# Revit family: Lighting-Suspended-Philips_Ledalite-TruGroove_LED
name_source: partatom
category: Lighting Fixtures
revit_build: Autodesk Revit 2017 (Build: 20160720_1515(x64)
units: mm (PartAtom-declared; Revit-internal decimal feet)

## family parameters
Cut with Voids When Loaded = No
Host = Face
Light Source = Yes
OmniClass Number = 23.80.70.11.14
OmniClass Title = General Luminaries, Directional
Part Type = Normal
Room Calculation Point = No
Round Connector Dimension = Use Diameter
Shared = No

## types (66) — shared parameters
Assembly Code = D5020200
Color Filter = 16777215
Default Elevation = 48"
Depth = 5"
Dimming Lamp Color Temperature Shift = <None>
Emit Shape Visible in Rendering = No
Emit from Rectangle Length = 48"
Emit from Rectangle Width = 3 7/32"
End Cap Depth = 3/16"
Housing Material Finish = Powder Coat-Signify-Titanium
Lamp = LED
Last Updated = 6/17/2015
Length = 48"
Lens Material Finish = Acrylic-Signify-White, Translucent
Manufacturer = Ledalite
Photometry Comments = Candela values are absolute.
Product Family = TruGroove
Product Page URL = http://www.lightingproducts.philips.com
Suspension Distance = 12"
Tilt Angle = -90.00°
URL = https://www.signify.com
Voltage = 120 V
Width = 3 7/32"
eCatalog URL = www.ledalite.com

## per-type parameters (varying)
| type | Apparent Load | Catalog Number | Description | Model | Photometric Web File |
| 2901LAEQN4 | 35 VA | 2901LAEQN4 | TruGroove Suspended Direct, LED, 4000K, 3200 Nominal Delivered Lumens, Symmetric MesoOptics, 4' | 2901LAEQN4 | 29x1LAEQN.ies |
| 2901LAEWN4 | 36 VA | 2901LAEWN4 | TruGroove Suspended Direct, LED, 4000K, 3200 Nominal Delivered Lumens, Asymmetric MesoOptics, 4' | 2901LAEWN4 | 29x1LAEWN.ies |
| 2901LAGQN4 | 24 VA | 2901LAGQN4 | TruGroove Suspended Direct, LED, 4000K, 2300 Nominal Delivered Lumens, Symmetric MesoOptics, 4' | 2901LAGQN4 | 29x1LAGQN.ies |
| 2901LAGWN4 | 24 VA | 2901LAGWN4 | TruGroove Suspended Direct, LED, 4000K, 2300 Nominal Delivered Lumens, Asymmetric MesoOptics, 4' | 2901LAGWN4 | 29x1LAGWN.ies |
| 2901LAKQN4 | 15 VA | 2901LAKQN4 | TruGroove Suspended Direct, LED, 4000K, 1500 Nominal Delivered Lumens, Symmetric MesoOptics, 4' | 2901LAKQN4 | 29x1LAKQN.ies |
| 2901LAKWN4 | 15 VA | 2901LAKWN4 | TruGroove Suspended Direct, LED, 4000K, 1500 Nominal Delivered Lumens, Asymmetric MesoOptics, 4' | 2901LAKWN4 | 29x1LAKWN.ies |
| 2901LBEQN4 | 35 VA | 2901LBEQN4 | TruGroove Suspended Direct, LED, 3500K, 3200 Nominal Delivered Lumens, Symmetric MesoOptics, 4' | 2901LBEQN4 | 29x1LBEQN.ies |
| 2901LBEWN4 | 35 VA | 2901LBEWN4 | TruGroove Suspended Direct, LED, 3500K, 3200 Nominal Delivered Lumens, Asymmetric MesoOptics, 4' | 2901LBEWN4 | 29x1LBEWN.ies |
| 2901LBGQN4 | 24 VA | 2901LBGQN4 | TruGroove Suspended Direct, LED, 3500K, 2300 Nominal Delivered Lumens, Symmetric MesoOptics, 4' | 2901LBGQN4 | 29x1LBGQN.ies |
| 2901LBGWN4 | 24 VA | 2911LBGWN4 | TruGroove Suspended Direct, LED, 3500K, 2300 Nominal Delivered Lumens, Asymmetric MesoOptics, 4' | 2911LBGWN4 | 29x1LBGWN.ies |
| 2901LBKQN4 | 15 VA | 2901LBKQN4 | TruGroove Suspended Direct, LED, 3500K, 1500 Nominal Delivered Lumens, Symmetric MesoOptics, 4' | 2901LBKQN4 | 29x1LBKQN.ies |
| 2901LBKWN4 | 15 VA | 2901LBKWN4 | TruGroove Suspended Direct, LED, 3500K, 1500 Nominal Delivered Lumens, Asymmetric MesoOptics, 4' | 2901LBKWN4 | 29x1LBKWN.ies |
| 2901LCEQN4 | 35 VA | 2901LCEQN4 | TruGroove Suspended Direct, LED, 3000K, 3200 Nominal Delivered Lumens, Symmetric MesoOptics, 4' | 2901LCEQN4 | 29x1LCEQN.ies |
| 2901LCEWN4 | 35 VA | 2901LCEWN4 | TruGroove Suspended Direct, LED, 3000K, 3200 Nominal Delivered Lumens, Asymmetric MesoOptics, 4' | 2901LCEWN4 | 29x1LCEWN.ies |
| 2901LCGQN4 | 24 VA | 2901LCGQN4 | TruGroove Suspended Direct, LED, 3000K, 2300 Nominal Delivered Lumens, Symmetric MesoOptics, 4' | 2901LCGQN4 | 29x1LCGQN.ies |
| 2901LCGWN4 | 24 VA | 2901LCGWN4 | TruGroove Suspended Direct, LED, 3000K, 2300 Nominal Delivered Lumens, Asymmetric MesoOptics, 4' | 2901LCGWN4 | 29x1LCGWN.ies |
| 2901LCKQN4 | 15 VA | 2901LCKQN4 | TruGroove Suspended Direct, LED, 3000K, 1500 Nominal Delivered Lumens, Symmetric MesoOptics, 4' | 2901LCKQN4 | 29x1LCKQN.ies |
| 2901LCKWN4 | 15 VA | 2901LCKWN4 | TruGroove Suspended Direct, LED, 3000K, 1500 Nominal Delivered Lumens, Asymmetric MesoOptics, 4' | 2901LCKWN4 | 29x1LCKWN.ies |
| 2903LACNQ4 | 41 VA | 2903LACNQ4 | TruGroove Suspended Indirect, LED, 4000K, 4800 Nominal Delivered Lumens, Symmetric MesoOptics, 4' | 2903LACNQ4 | 29x3LACNQ.ies |
| 2903LACNW4 | 41 VA | 2903LACNW4 | TruGroove Suspended Indirect, LED, 4000K, 4800 Nominal Delivered Lumens, Asymmetric MesoOptics, 4' | 2903LACNW4 | 29x3LACNW.ies |
| 2903LAENQ4 | 26 VA | 2903LAENQ4 | TruGroove Suspended Indirect, LED, 4000K, 3200 Nominal Delivered Lumens, Symmetric MesoOptics, 4' | 2903LAENQ4 | 29x3LAENQ.ies |
| 2903LAENW4 | 26 VA | 2903LAENW4 | TruGroove Suspended Indirect, LED, 4000K, 3200 Nominal Delivered Lumens, Asymmetric MesoOptics, 4' | 2903LAENW4 | 29x3LAENW.ies |
| 2903LBCNQ4 | 41 VA | 2903LBCNQ4 | TruGroove Suspended Indirect, LED, 3500K, 4800 Nominal Delivered Lumens, Symmetric MesoOptics, 4' | 2903LBCNQ4 | 29x3LBCNQ.ies |
| 2903LBCNW4 | 41 VA | 2903LBCNW4 | TruGroove Suspended Indirect, LED, 3500K, 4800 Nominal Delivered Lumens, Asymmetric MesoOptics, 4' | 2903LBCNW4 | 29x3LBCNW.ies |
| 2903LBENQ4 | 26 VA | 2903LBENQ4 | TruGroove Suspended Indirect, LED, 3500K, 3200 Nominal Delivered Lumens, Symmetric MesoOptics, 4' | 2903LBENQ4 | 29x3LBENQ.ies |
| 2903LBENW4 | 26 VA | 2903LBENW4 | TruGroove Suspended Indirect, LED, 3500K, 3200 Nominal Delivered Lumens, Asymmetric MesoOptics, 4' | 2903LBENW4 | 29x3LBENW.ies |
| 2903LCCNQ4 | 41 VA | 2903LCCNQ4 | TruGroove Suspended Indirect, LED, 3000K, 4800 Nominal Delivered Lumens, Symmetric MesoOptics, 4' | 2903LCCNQ4 | 29x3LCCNQ.ies |
| 2903LCCNW4 | 41 VA | 2903LCCNQ4 | TruGroove Suspended Indirect, LED, 3000K, 4800 Nominal Delivered Lumens, Asymmetric MesoOptics, 4' | 2903LCCNQ4 | 29x3LCCNQ.ies |
| 2903LCENQ4 | 26 VA | 2903LCENQ4 | TruGroove Suspended Indirect, LED, 3000K, 3200 Nominal Delivered Lumens, Symmetric MesoOptics, 4' | 2903LCENQ4 | 29x3LCENQ.ies |
| 2903LCENW4 | 26 VA | 2903LCENW4 | TruGroove Suspended Indirect, LED, 3000K, 3200 Nominal Delivered Lumens, Asymmetric MesoOptics, 4' | 2903LCENW4 | 29x3LCENW.ies |
| 2905LABQQ4 | 47 VA | 2905LABQQ4 | TruGroove Suspended Indirect/Direct, LED, 4000K, 5200 Nominal Delivered Lumens, Symmetric MesoOptics Top & Bottom, 4' | 2905LABQQ4 | 29x5LABQQ.ies |
| 2905LABWW4 | 47 VA | 2905LABWW4 | TruGroove Suspended Indirect/Direct, LED, 4000K, 5200 Nominal Delivered Lumens, Asymmetric MesoOptics Top and Bottom, 4' | 2905LABWW4 | 29x5LABWW.ies |
| 2905LACQQ4 | 41 VA | 2905LACQQ4 | TruGroove Suspended Indirect/Direct, LED, 4000K, 4600 Nominal Delivered Lumens, Symmetric MesoOptics Top & Bottom, 4' | 2905LACQQ4 | 29x5LACQQ.ies |
| 2905LACWW4 | 41 VA | 2905LACWW4 | TruGroove Suspended Indirect/Direct, LED, 4000K, 4600 Nominal Delivered Lumens, Asymmetric MesoOptics Top and Bottom, 4' | 2905LACWW4 | 29x5LACWW.ies |
| 2905LADQQ4 | 29 VA | 2905LADQQ4 | TruGroove Suspended Indirect/Direct, LED, 4000K, 3500 Nominal Delivered Lumens, Symmetric MesoOptics Top & Bottom, 4' | 2905LADQQ4 | 29x5LADQQ.ies |
| 2905LADWW4 | 29 VA | 2905LADWW4 | TruGroove Suspended Indirect/Direct, LED, 4000K, 3500 Nominal Delivered Lumens, Asymmetric MesoOptics Top and Bottom, 4' | 2905LADWW4 | 29x5LADWW.ies |
| 2905LBBQQ4 | 46 VA | 2905LBBQQ4 | TruGroove Suspended Indirect/Direct, LED, 3500K, 5200 Nominal Delivered Lumens, Symmetric MesoOptics Top & Bottom, 4' | 2905LBBQQ4 | 29x5LBBQQ.ies |
| 2905LBBWW4 | 46 VA | 2905LBBWW4 | TruGroove Suspended Indirect/Direct, LED, 3500K, 5200 Nominal Delivered Lumens, Asymmetric MesoOptics Top and Bottom, 4' | 2905LBBWW4 | 29x5LBBWW.ies |
| 2905LBCQQ4 | 41 VA | 2905LBCQQ4 | TruGroove Suspended Indirect/Direct, LED, 3500K, 4600 Nominal Delivered Lumens, Symmetric MesoOptics Top & Bottom, 4' | 2905LBCQQ4 | 29x5LBCQQ.ies |
| 2905LBCWW4 | 41 VA | 2905LBCWW4 | TruGroove Suspended Indirect/Direct, LED, 3500K, 4600 Nominal Delivered Lumens, Asymmetric MesoOptics Top and Bottom, 4' | 2905LBCWW4 | 29x5LBCWW.ies |
| 2905LBDQQ4 | 29 VA | 2905LBDQQ4 | TruGroove Suspended Indirect/Direct, LED, 3500K, 3500 Nominal Delivered Lumens, Symmetric MesoOptics Top & Bottom, 4' | 2905LBDQQ4 | 29x5LBDQQ.ies |
| 2905LBDWW4 | 29 VA | 2905LBDWW4 | TruGroove Suspended Indirect/Direct, LED, 3500K, 3500 Nominal Delivered Lumens, Asymmetric MesoOptics Top and Bottom, 4' | 2905LBDWW4 | 29x5LBDWW.ies |
| 2905LCBQQ4 | 46 VA | 2905LCBQQ4 | TruGroove Suspended Indirect/Direct, LED, 3000K, 5200 Nominal Delivered Lumens, Symmetric MesoOptics Top & Bottom, 4' | 2905LCBQQ4 | 29x5LCBQQ.ies |
| 2905LCBWW4 | 46 VA | 2905LCBWW4 | TruGroove Suspended Indirect/Direct, LED, 3000K, 5200 Nominal Delivered Lumens, Asymmetric MesoOptics Top and Bottom, 4' | 2905LCBWW4 | 29x5LCBWW.ies |
| 2905LCCQQ4 | 41 VA | 2905LCCQQ4 | TruGroove Suspended Indirect/Direct, LED, 3000K, 4600 Nominal Delivered Lumens, Symmetric MesoOptics Top & Bottom, 4' | 2905LCCQQ4 | 29x5LCCQQ.ies |
| 2905LCCWW4 | 41 VA | 2905LCCWW4 | TruGroove Suspended Indirect/Direct, LED, 3000K, 4600 Nominal Delivered Lumens, Asymmetric MesoOptics Top and Bottom, 4' | 2905LCCWW4 | 29x5LCCWW.ies |
| 2905LCDQQ4 | 29 VA | 2905LCDQQ4 | TruGroove Suspended Indirect/Direct, LED, 3000K, 3500 Nominal Delivered Lumens, Symmetric MesoOptics Top & Bottom, 4' | 2905LCDQQ4 | 29x5LCDQQ.ies |
| 2905LCDWW4 | 29 VA | 2905LCDWW4 | TruGroove Suspended Indirect/Direct, LED, 3000K, 3500 Nominal Delivered Lumens, Asymmetric MesoOptics Top and Bottom, 4' | 2905LCDWW4 | 29x5LCDWW.ies |
| 2906LABQQ4 | 51 VA | 2906LABQQ4 | TruGroove Suspended Direct/Indirect, LED, 4000K, 5200 Nominal Delivered Lumens, Symmetirc MesoOptics Top and Bottom, 4' | 2906LABQQ4 | 29x6LABQQ.ies |
| 2906LABWW4 | 51 VA | 2906LABWW4 | TruGroove Suspended Direct/Indirect, LED, 4000K, 5200 Nominal Delivered Lumens, Asymmetirc MesoOptics Top and Bottom, 4' | 2906LABWW4 | 29x6LABWW.ies |
| 2906LACQQ4 | 46 VA | 2906LACQQ4 | TruGroove Suspended Direct/Indirect, LED, 4000K, 4600 Nominal Delivered Lumens, Symmetirc MesoOptics Top and Bottom, 4' | 2906LACQQ4 | 29x6LACQQ.ies |
| 2906LACWW4 | 46 VA | 2906LACWW4 | TruGroove Suspended Direct/Indirect, LED, 4000K, 4600 Nominal Delivered Lumens, Asymmetirc MesoOptics Top and Bottom, 4' | 2906LACWW4 | 29x6LACWW.ies |
| 2906LADQQ4 | 35 VA | 2906LADQQ4 | TruGroove Suspended Direct/Indirect, LED, 4000K, 3500 Nominal Delivered Lumens, Symmetirc MesoOptics Top and Bottom, 4' | 2906LADQQ4 | 29x6LADQQ.ies |
| 2906LADWW4 | 35 VA | 2906LADWW4 | TruGroove Suspended Direct/Indirect, LED, 4000K, 3500 Nominal Delivered Lumens, Asymmetirc MesoOptics Top and Bottom, 4' | 2906LADWW4 | 29x6LADWW.ies |
| 2906LBBQQ4 | 50 VA | 2906LBBQQ4 | TruGroove Suspended Direct/Indirect, LED, 3500K, 5200 Nominal Delivered Lumens, Symmetirc MesoOptics Top and Bottom, 4' | 2906LBBQQ4 | 29x6LBBQQ.ies |
| 2906LBBWW4 | 50 VA | 2906LBBWW4 | TruGroove Suspended Direct/Indirect, LED, 3500K, 5200 Nominal Delivered Lumens, Asymmetirc MesoOptics Top and Bottom, 4' | 2906LBBWW4 | 29x6LBBWW.ies |
| 2906LBCQQ4 | 46 VA | 2906LBCQQ4 | TruGroove Suspended Direct/Indirect, LED, 3500K, 4600 Nominal Delivered Lumens, Symmetirc MesoOptics Top and Bottom, 4' | 2906LBCQQ4 | 29x6LBCQQ.ies |
| 2906LBCWW4 | 46 VA | 2906LBCWW4 | TruGroove Suspended Direct/Indirect, LED, 3500K, 4600 Nominal Delivered Lumens, Asymmetirc MesoOptics Top and Bottom, 4' | 2906LBCWW4 | 29x6LBCWW.ies |
| 2906LBDQQ4 | 35 VA | 2906LBDQQ4 | TruGroove Suspended Direct/Indirect, LED, 3500K, 3500 Nominal Delivered Lumens, Symmetirc MesoOptics Top and Bottom, 4' | 2906LBDQQ4 | 29x6LBDQQ.ies |
| 2906LBDWW4 | 35 VA | 2906LBDWW4 | TruGroove Suspended Direct/Indirect, LED, 3500K, 3500 Nominal Delivered Lumens, Asymmetirc MesoOptics Top and Bottom, 4' | 2906LBDWW4 | 29x6LBDWW.ies |
| 2906LCBQQ4 | 50 VA | 2906LCBQQ1 | TruGroove Suspended Direct/Indirect, LED, 3000K, 5200 Nominal Delivered Lumens, Symmetirc MesoOptics Top and Bottom, 4' | 2906LCBQQ1 | 29x6LCBQQ.ies |
| 2906LCBWW4 | 50 VA | 2906LCBWW4 | TruGroove Suspended Direct/Indirect, LED, 3000K, 5200 Nominal Delivered Lumens, Asymmetirc MesoOptics Top and Bottom, 4' | 2906LCBWW4 | 29x6LCBWW.ies |
| 2906LCCQQ4 | 46 VA | 2906LCCQQ4 | TruGroove Suspended Direct/Indirect, LED, 3000K, 4600 Nominal Delivered Lumens, Symmetirc MesoOptics Top and Bottom, 4' | 2906LCCQQ4 | 29x6LCCQQ.ies |
| 2906LCCWW4 | 46 VA | 2906LCCWW4 | TruGroove Suspended Direct/Indirect, LED, 3000K, 4600 Nominal Delivered Lumens, Asymmetirc MesoOptics Top and Bottom, 4' | 2906LCCWW4 | 29x6LCCWW.ies |
| 2906LCDQQ4 | 35 VA | 2906LCDQQ4 | TruGroove Suspended Direct/Indirect, LED, 3000K, 3500 Nominal Delivered Lumens, Symmetirc MesoOptics Top and Bottom, 4' | 2906LCDQQ4 | 29x6LCDQQ.ies |
| 2906LCDWW4 | 35 VA | 2906LCDWW4 | TruGroove Suspended Direct/Indirect, LED, 3000K, 3500 Nominal Delivered Lumens, Asymmetirc MesoOptics Top and Bottom, 4' | 2906LCDWW4 | 29x6LCDWW.ies |

## geometry (parser evidence)
native form markers: Blend x8, Sweep x5
no freeform markers — native parametric forms only
